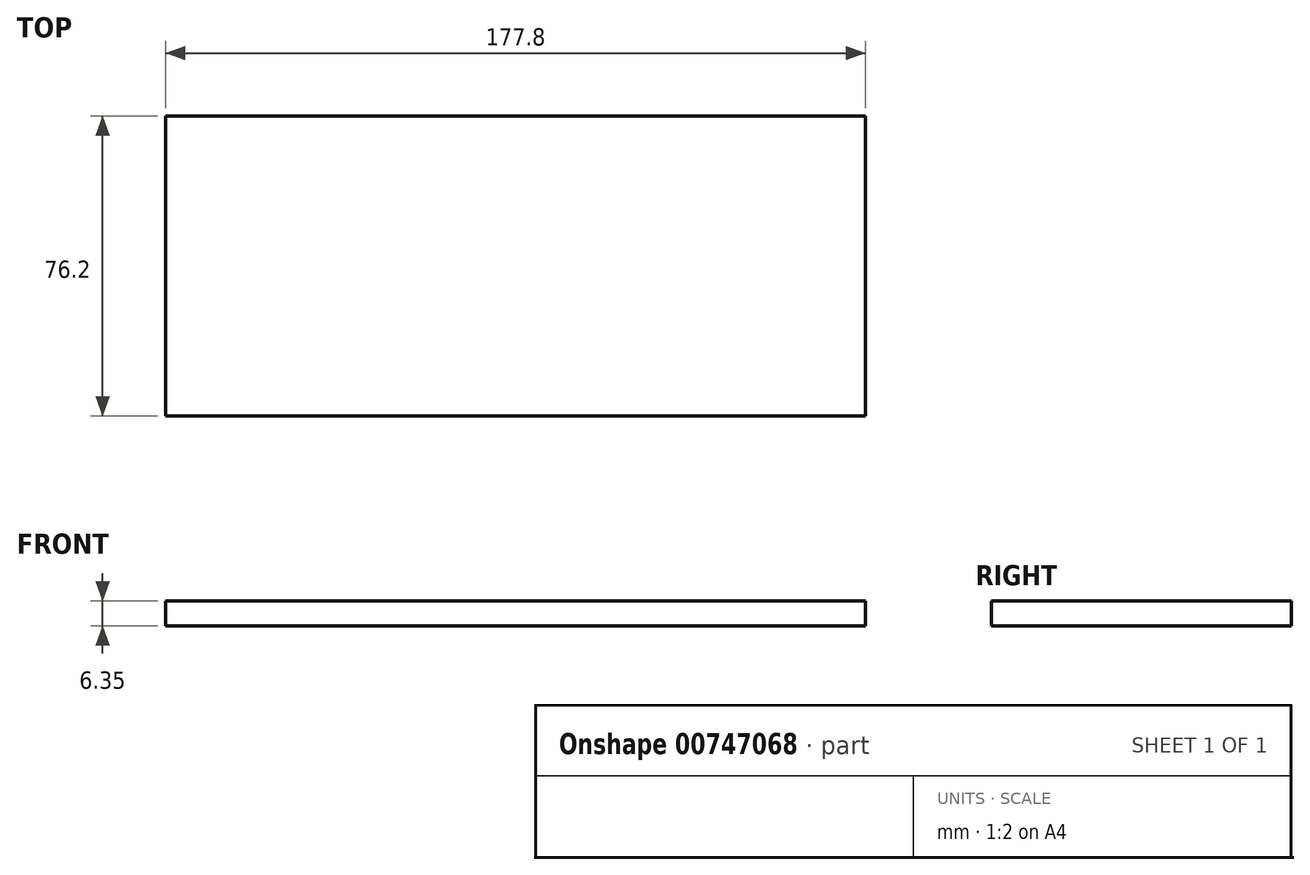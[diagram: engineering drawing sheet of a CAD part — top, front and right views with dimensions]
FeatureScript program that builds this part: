
annotation { "Feature Type Name" : "Feature", "Feature Type Description" : "" }
export const myFeature = defineFeature(function(context is Context, id is Id, definition is map)
    precondition{}
    {
        {
            var Q0;
            Q0=qCreatedBy(makeId("Top.planeOp"),FACE);
            var sketch = newSketch(context, id + "F0", { "sketchPlane" : qUnion([Q0])});
            skLineSegment(sketch, "E0.bottom", {"start": v(-77.36, 76.2) * mm, "end": v(100.44, 76.2) * mm});
            skLineSegment(sketch, "E0.top", {"start": v(-77.36, 0) * mm, "end": v(100.44, 0) * mm});
            skLineSegment(sketch, "E0.left", {"start": v(-77.36, 76.2) * mm, "end": v(-77.36, 0) * mm});
            skLineSegment(sketch, "E0.right", {"start": v(100.44, 76.2) * mm, "end": v(100.44, 0) * mm});
            skSolve(sketch);
        }
        {
            var Q0;
            Q0 = qSketchRegion(id + "F0", true);
            extrude(context, id + "F1", {"entities" : qUnion([Q0]), "depth" : 6.35 * mm, "offsetDistance" : 25.4 * mm});
        }
    });
